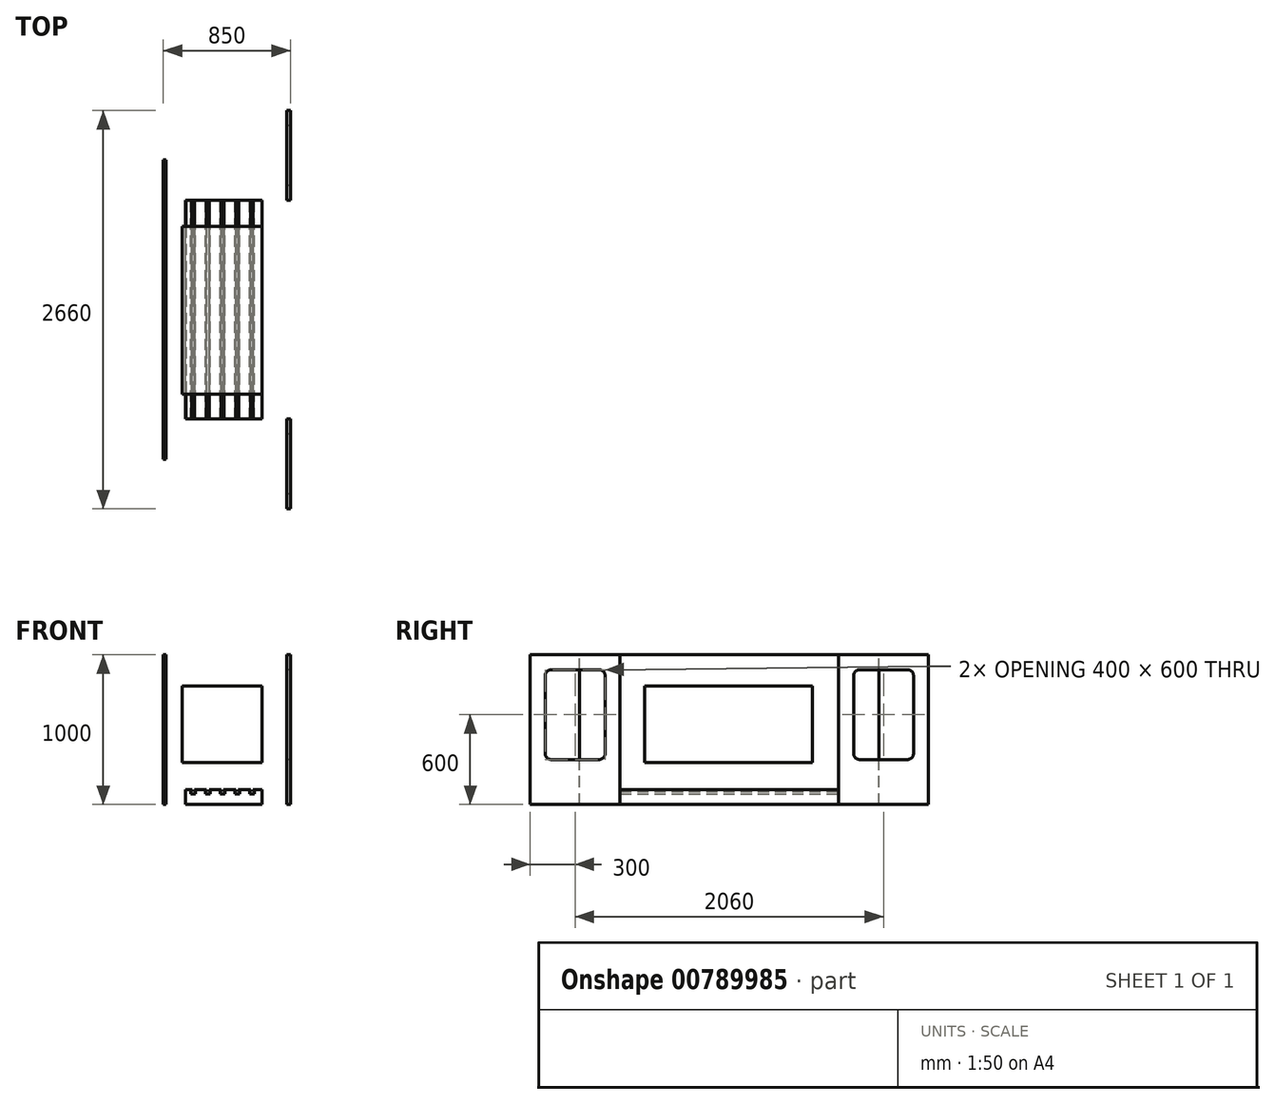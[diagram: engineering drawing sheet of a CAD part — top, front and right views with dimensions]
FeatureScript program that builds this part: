
annotation { "Feature Type Name" : "Feature", "Feature Type Description" : "" }
export const myFeature = defineFeature(function(context is Context, id is Id, definition is map)
    precondition{}
    {
        {
            var Q0;
            Q0=qCreatedBy(makeId("Front.planeOp"),FACE);
            var sketch = newSketch(context, id + "F0", { "sketchPlane" : qUnion([Q0])});
            skLineSegment(sketch, "E0.bottom", {"start": v(0, 0) * mm, "end": v(510, 0) * mm});
            skLineSegment(sketch, "E0.top", {"start": v(0, 100) * mm, "end": v(42, 100) * mm});
            skLineSegment(sketch, "E0.left", {"start": v(0, 0) * mm, "end": v(0, 100) * mm});
            skLineSegment(sketch, "E0.right", {"start": v(510, 0) * mm, "end": v(510, 100) * mm});
            skPoint(sketch, "E1.middle", {"position": v(0, 100) * mm});
            skLineSegment(sketch, "E2.top", {"start": v(34, 70) * mm, "end": v(66, 70) * mm});
            skLineSegment(sketch, "E2.left", {"start": v(34, 85) * mm, "end": v(34, 70) * mm});
            skLineSegment(sketch, "E2.right", {"start": v(66, 84.98) * mm, "end": v(66, 70) * mm});
            skLineSegment(sketch, "E3.top", {"start": v(34, 85) * mm, "end": v(42, 85) * mm});
            skLineSegment(sketch, "E3.right", {"start": v(42, 100) * mm, "end": v(42, 85) * mm});
            skLineSegment(sketch, "E4.top", {"start": v(66, 84.98) * mm, "end": v(58, 84.98) * mm});
            skLineSegment(sketch, "E5", {"start": v(58, 84.98) * mm, "end": v(58, 100) * mm});
            skLineSegment(sketch, "E6.1.0.0", {"start": v(140, 100) * mm, "end": v(140, 85) * mm});
            skLineSegment(sketch, "E6.1.0.1", {"start": v(132, 70) * mm, "end": v(164, 70) * mm});
            skLineSegment(sketch, "E6.1.0.2", {"start": v(156, 84.98) * mm, "end": v(156, 100) * mm});
            skLineSegment(sketch, "E6.1.0.3", {"start": v(164, 84.98) * mm, "end": v(164, 70) * mm});
            skLineSegment(sketch, "E6.1.0.4", {"start": v(132, 85) * mm, "end": v(132, 70) * mm});
            skLineSegment(sketch, "E6.1.0.5", {"start": v(164, 84.98) * mm, "end": v(156, 84.98) * mm});
            skLineSegment(sketch, "E6.1.0.6", {"start": v(132, 85) * mm, "end": v(140, 85) * mm});
            skLineSegment(sketch, "E6.2.0.0", {"start": v(238, 100) * mm, "end": v(238, 85) * mm});
            skLineSegment(sketch, "E6.2.0.1", {"start": v(230, 70) * mm, "end": v(262, 70) * mm});
            skLineSegment(sketch, "E6.2.0.2", {"start": v(254, 84.98) * mm, "end": v(254, 100) * mm});
            skLineSegment(sketch, "E6.2.0.3", {"start": v(262, 84.98) * mm, "end": v(262, 70) * mm});
            skLineSegment(sketch, "E6.2.0.4", {"start": v(230, 85) * mm, "end": v(230, 70) * mm});
            skLineSegment(sketch, "E6.2.0.5", {"start": v(262, 84.98) * mm, "end": v(254, 84.98) * mm});
            skLineSegment(sketch, "E6.2.0.6", {"start": v(230, 85) * mm, "end": v(238, 85) * mm});
            skLineSegment(sketch, "E6.3.0.0", {"start": v(336, 100) * mm, "end": v(336, 85) * mm});
            skLineSegment(sketch, "E6.3.0.1", {"start": v(328, 70) * mm, "end": v(360, 70) * mm});
            skLineSegment(sketch, "E6.3.0.2", {"start": v(352, 84.98) * mm, "end": v(352, 100) * mm});
            skLineSegment(sketch, "E6.3.0.3", {"start": v(360, 84.98) * mm, "end": v(360, 70) * mm});
            skLineSegment(sketch, "E6.3.0.4", {"start": v(328, 85) * mm, "end": v(328, 70) * mm});
            skLineSegment(sketch, "E6.3.0.5", {"start": v(360, 84.98) * mm, "end": v(352, 84.98) * mm});
            skLineSegment(sketch, "E6.3.0.6", {"start": v(328, 85) * mm, "end": v(336, 85) * mm});
            skLineSegment(sketch, "E6.4.0.0", {"start": v(434, 100) * mm, "end": v(434, 85) * mm});
            skLineSegment(sketch, "E6.4.0.1", {"start": v(426, 70) * mm, "end": v(458, 70) * mm});
            skLineSegment(sketch, "E6.4.0.2", {"start": v(450, 84.98) * mm, "end": v(450, 100) * mm});
            skLineSegment(sketch, "E6.4.0.3", {"start": v(458, 84.98) * mm, "end": v(458, 70) * mm});
            skLineSegment(sketch, "E6.4.0.4", {"start": v(426, 85) * mm, "end": v(426, 70) * mm});
            skLineSegment(sketch, "E6.4.0.5", {"start": v(458, 84.98) * mm, "end": v(450, 84.98) * mm});
            skLineSegment(sketch, "E6.4.0.6", {"start": v(426, 85) * mm, "end": v(434, 85) * mm});
            skLineSegment(sketch, "E6.direction1", {"start": v(34, 70) * mm, "end": v(132, 70) * mm, "construction": true});
            skLineSegment(sketch, "E7.trimOffspring", {"start": v(58, 100) * mm, "end": v(140, 100) * mm});
            skLineSegment(sketch, "E8.trimOffspring", {"start": v(156, 100) * mm, "end": v(238, 100) * mm});
            skLineSegment(sketch, "E9.trimOffspring", {"start": v(254, 100) * mm, "end": v(336, 100) * mm});
            skLineSegment(sketch, "E10.trimOffspring", {"start": v(352, 100) * mm, "end": v(434, 100) * mm});
            skLineSegment(sketch, "E11.trimOffspring", {"start": v(450, 100) * mm, "end": v(510, 100) * mm});
            skSolve(sketch);
        }
        {
            var Q0;
            Q0 = qSketchRegion(id + "F0", true);
            extrude(context, id + "F1", {"entities" : qUnion([Q0]), "depth" : 1460 * mm, "offsetDistance" : 25 * mm});
        }
        {
            var Q0;
            Q0=makeQuery(id+"F1.opExtrude","SWEPT_EDGE",EDGE,{"disambiguationData":[OSD([sQuery(id+"F0.wireOp",EDGE,"E0.top"),sQuery(id+"F0.wireOp",EDGE,"E3.right")])]});
            var Q1;
            Q1=makeQuery(id+"F1.opExtrude","SWEPT_EDGE",EDGE,{"disambiguationData":[OSD([sQuery(id+"F0.wireOp",EDGE,"E5"),sQuery(id+"F0.wireOp",EDGE,"E7.trimOffspring")])]});
            var Q2;
            Q2=makeQuery(id+"F1.opExtrude","SWEPT_EDGE",EDGE,{"disambiguationData":[OSD([sQuery(id+"F0.wireOp",EDGE,"E6.1.0.0"),sQuery(id+"F0.wireOp",EDGE,"E7.trimOffspring")])]});
            var Q3;
            Q3=makeQuery(id+"F1.opExtrude","SWEPT_EDGE",EDGE,{"disambiguationData":[OSD([sQuery(id+"F0.wireOp",EDGE,"E6.1.0.2"),sQuery(id+"F0.wireOp",EDGE,"E8.trimOffspring")])]});
            var Q4;
            Q4=makeQuery(id+"F1.opExtrude","SWEPT_EDGE",EDGE,{"disambiguationData":[OSD([sQuery(id+"F0.wireOp",EDGE,"E6.2.0.0"),sQuery(id+"F0.wireOp",EDGE,"E8.trimOffspring")])]});
            var Q5;
            Q5=makeQuery(id+"F1.opExtrude","SWEPT_EDGE",EDGE,{"disambiguationData":[OSD([sQuery(id+"F0.wireOp",EDGE,"E6.2.0.2"),sQuery(id+"F0.wireOp",EDGE,"E9.trimOffspring")])]});
            var Q6;
            Q6=makeQuery(id+"F1.opExtrude","SWEPT_EDGE",EDGE,{"disambiguationData":[OSD([sQuery(id+"F0.wireOp",EDGE,"E6.3.0.0"),sQuery(id+"F0.wireOp",EDGE,"E9.trimOffspring")])]});
            var Q7;
            Q7=makeQuery(id+"F1.opExtrude","SWEPT_EDGE",EDGE,{"disambiguationData":[OSD([sQuery(id+"F0.wireOp",EDGE,"E6.3.0.2"),sQuery(id+"F0.wireOp",EDGE,"E10.trimOffspring")])]});
            var Q8;
            Q8=makeQuery(id+"F1.opExtrude","SWEPT_EDGE",EDGE,{"disambiguationData":[OSD([sQuery(id+"F0.wireOp",EDGE,"E6.4.0.0"),sQuery(id+"F0.wireOp",EDGE,"E10.trimOffspring")])]});
            var Q9;
            Q9=makeQuery(id+"F1.opExtrude","SWEPT_EDGE",EDGE,{"disambiguationData":[OSD([sQuery(id+"F0.wireOp",EDGE,"E6.4.0.2"),sQuery(id+"F0.wireOp",EDGE,"E11.trimOffspring")])]});
            var Q10;
            Q10=makeQuery(id+"F1.opExtrude","SWEPT_EDGE",EDGE,{"disambiguationData":[OSD([sQuery(id+"F0.wireOp",EDGE,"E0.right"),sQuery(id+"F0.wireOp",EDGE,"E11.trimOffspring")])]});
            var Q11;
            Q11=makeQuery(id+"F1.opExtrude","SWEPT_EDGE",EDGE,{"disambiguationData":[OSD([sQuery(id+"F0.wireOp",EDGE,"E0.top"),sQuery(id+"F0.wireOp",EDGE,"E0.left")])]});
            chamfer(context, id + "F2", {"entities" : qUnion([Q0, Q1, Q2, Q3, Q4, Q5, Q6, Q7, Q8, Q9, Q10, Q11]), "width" : 1 * mm, "tangentPropagation" : true});
        }
        {
            var Q0;
            Q0=qCreatedBy(makeId("Right.planeOp"),FACE);
            cPlane(context, id + "F3", {"entities" : qUnion([Q0]), "cplaneType" : CPlaneType.OFFSET, "offset" : 130 * mm, "oppositeDirection" : true, "width" : 150 * mm, "height" : 150 * mm});
        }
        {
            var Q0;
            Q0=qCreatedBy(id+"F3.planeOp",FACE);
            var sketch = newSketch(context, id + "F4", { "sketchPlane" : qUnion([Q0])});
            skLineSegment(sketch, "E12.top", {"start": v(270, 1000) * mm, "end": v(-1730, 1000) * mm});
            skLineSegment(sketch, "E12.left", {"start": v(270, 0) * mm, "end": v(270, 1000) * mm});
            skLineSegment(sketch, "E12.right", {"start": v(-1730, 0) * mm, "end": v(-1730, 1000) * mm});
            skLineSegment(sketch, "E13", {"start": v(-1730, 0) * mm, "end": v(270, 0) * mm});
            skSolve(sketch);
        }
        {
            var Q0;
            Q0=makeQuery(id+"F4.imprint","IMPRINT",FACE,{"disambiguationData":[TD([[makeQuery(id+"F4.imprint","IMPRINT",EDGE,{"derivedFrom":sQuery(id+"F4.wireOp",EDGE,"E12.top")}),1.0]])]});
            extrude(context, id + "F5", {"entities" : qUnion([Q0]), "oppositeDirection" : true, "depth" : 20 * mm, "offsetDistance" : 25 * mm});
        }
        {
            var Q0;
            Q0=qCreatedBy(makeId("Right.planeOp"),FACE);
            var sketch = newSketch(context, id + "F6", { "sketchPlane" : qUnion([Q0])});
            skLineSegment(sketch, "E14.bottom", {"start": v(-175, 280) * mm, "end": v(-1295, 280) * mm});
            skLineSegment(sketch, "E14.top", {"start": v(-175, 790) * mm, "end": v(-1295, 790) * mm});
            skLineSegment(sketch, "E14.left", {"start": v(-175, 280) * mm, "end": v(-175, 790) * mm});
            skLineSegment(sketch, "E14.right", {"start": v(-1295, 280) * mm, "end": v(-1295, 790) * mm});
            skSolve(sketch);
        }
        {
            var Q0;
            Q0=makeQuery(id+"F6.imprint","IMPRINT",FACE,{"disambiguationData":[TD([[makeQuery(id+"F6.imprint","IMPRINT",EDGE,{"derivedFrom":sQuery(id+"F6.wireOp",EDGE,"E14.bottom")}),-1.0]])]});
            extrude(context, id + "F7", {"entities" : qUnion([Q0]), "depth" : 510 * mm, "offsetDistance" : 25 * mm, "hasSecondDirection" : true, "secondDirectionOppositeDirection" : true, "secondDirectionDepth" : 25 * mm});
        }
        {
            var Q0;
            Q0=qCreatedBy(makeId("Right.planeOp"),FACE);
            cPlane(context, id + "F8", {"entities" : qUnion([Q0]), "cplaneType" : CPlaneType.OFFSET, "offset" : 675 * mm, "width" : 150 * mm, "height" : 150 * mm});
        }
        {
            var Q0;
            Q0=qCreatedBy(id+"F8.planeOp",FACE);
            var sketch = newSketch(context, id + "F9", { "sketchPlane" : qUnion([Q0])});
            skLineSegment(sketch, "E15.bottom", {"start": v(0, 0) * mm, "end": v(600, 0) * mm});
            skLineSegment(sketch, "E15.top", {"start": v(0, 1000) * mm, "end": v(600, 1000) * mm});
            skLineSegment(sketch, "E15.left", {"start": v(0, 0) * mm, "end": v(0, 1000) * mm});
            skLineSegment(sketch, "E15.right", {"start": v(600, 0) * mm, "end": v(600, 1000) * mm});
            skLineSegment(sketch, "E16.bottom", {"start": v(140, 900) * mm, "end": v(460, 900) * mm});
            skLineSegment(sketch, "E16.top", {"start": v(140, 300) * mm, "end": v(460, 300) * mm});
            skLineSegment(sketch, "E16.left", {"start": v(100, 860) * mm, "end": v(100, 340) * mm});
            skLineSegment(sketch, "E16.right", {"start": v(500, 860) * mm, "end": v(500, 340) * mm});
            skPoint(sketch, "E17.visualSharp", {"position": v(100, 900) * mm});
            skArc(sketch, "E17.filletArc", {"start": v(140, 900) * mm, "mid": v(111.72, 888.28) * mm, "end": v(100, 860) * mm});
            skPoint(sketch, "E18.visualSharp", {"position": v(500, 900) * mm});
            skArc(sketch, "E18.filletArc", {"start": v(500, 860) * mm, "mid": v(488.28, 888.28) * mm, "end": v(460, 900) * mm});
            skPoint(sketch, "E19.visualSharp", {"position": v(500, 300) * mm});
            skArc(sketch, "E19.filletArc", {"start": v(460, 300) * mm, "mid": v(488.28, 311.72) * mm, "end": v(500, 340) * mm});
            skPoint(sketch, "E20.visualSharp", {"position": v(100, 300) * mm});
            skArc(sketch, "E20.filletArc", {"start": v(100, 340) * mm, "mid": v(111.72, 311.72) * mm, "end": v(140, 300) * mm});
            skSolve(sketch);
        }
        {
            var Q0;
            Q0=makeQuery(id+"F9.imprint","IMPRINT",FACE,{"disambiguationData":[TD([[makeQuery(id+"F9.imprint","IMPRINT",EDGE,{"derivedFrom":sQuery(id+"F9.wireOp",EDGE,"E15.bottom")}),1.0]])]});
            extrude(context, id + "F10", {"entities" : qUnion([Q0]), "depth" : 25 * mm, "offsetDistance" : 25 * mm});
        }
        {
            var Q0;
            Q0=qCreatedBy(makeId("Front.planeOp"),FACE);
            cPlane(context, id + "F11", {"entities" : qUnion([Q0]), "cplaneType" : CPlaneType.OFFSET, "offset" : 730 * mm, "width" : 150 * mm, "height" : 150 * mm});
        }
        {
            var Q0;
            Q0=makeQuery(id+"F10.opExtrude","SWEPT_BODY",BODY,{"disambiguationData":[OSD([sQuery(id+"F9.wireOp",EDGE,"E15.bottom"),sQuery(id+"F9.wireOp",EDGE,"E15.top"),sQuery(id+"F9.wireOp",EDGE,"E15.left"),sQuery(id+"F9.wireOp",EDGE,"E15.right"),sQuery(id+"F9.wireOp",EDGE,"E16.bottom"),sQuery(id+"F9.wireOp",EDGE,"E16.top"),sQuery(id+"F9.wireOp",EDGE,"E16.left"),sQuery(id+"F9.wireOp",EDGE,"E16.right"),sQuery(id+"F9.wireOp",EDGE,"E17.filletArc"),sQuery(id+"F9.wireOp",EDGE,"E18.filletArc"),sQuery(id+"F9.wireOp",EDGE,"E19.filletArc"),sQuery(id+"F9.wireOp",EDGE,"E20.filletArc")])]});
            var Q1;
            Q1=qCreatedBy(id+"F11.planeOp",FACE);
            mirror(context, id + "F12", {"entities" : qUnion([Q0]), "mirrorPlane" : qUnion([Q1])});
        }
    });
